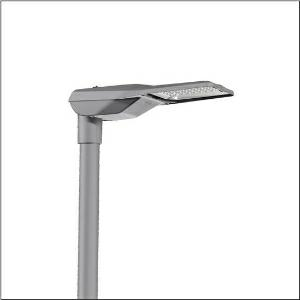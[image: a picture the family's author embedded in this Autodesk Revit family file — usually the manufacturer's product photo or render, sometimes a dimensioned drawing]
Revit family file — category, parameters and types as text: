
# Revit family: streetlight_sl_21_mini___st1_0ab_5xe2m33s08hb_60c9
name_source: partatom
category: Lighting Fixtures
units: mm (PartAtom-declared; Revit-internal decimal feet)

## family parameters
Cut with Voids When Loaded = No
Host = Face
Light Source = No
Part Type = Normal
Room Calculation Point = No
Round Connector Dimension = Use Diameter
Shared = No

## types (1)
- --- (1 x LED, 7960 lm, 66 W, 3000K)
    Apparent Load = 66 VA
    CIE Flux Codes = 38 73 97 100 100
    Color Rendering = 70
    Color Temperature = 3000K
    Default Elevation = 1800 mm
    Description = Streetlight SL 21 mini, mast luminaire, primary light control with lens, of PMMA, primary optical cover: cover, of toughened safety glass, transparent, light distribution: ST1.0aB, light emission: direct distribution, primary light characteristic: asymmetric, installation type: side-entry, post-top, LED, High Power LED, rated luminous flux: 7.960lm, luminous efficacy: 121lm/W, light colour: 730, colour temperature: 3000K, control gear: D4i, control: flexible luminous flux parameterisation, time-dependent luminous flux control, constant luminous flux control, overheat protection, pre-setting: logarithmic dimming characteristic, mains connection: 220..240V, AC, 50/60Hz, start of lifetime: 66W, end of service life: 69W, reduction: 30W, luminaire housing, of diecast aluminium, powder-coated, SITECO metallic grey (DB 702S), corrosivity category C5 high according to DIN EN ISO 12944, please order mast flange separately, inclination adjustable: 0°, 5°, 10°, 15°, sealing non-destructively replaceable, multi-level sealing system, length: 628mm, width: 235mm, height: 110mm, mast flange for spigot size: 42mm (side-entry): 5XC10008XM4, 60/48mm (side-entry/post-top): 5XC10108XM2, 76/60mm (side-entry/post-top): 5XC10108XM1, mounting height: 4..8m, Smart Interface above, protection rating (complete): IP66, insulation class (complete): insulation class II (safety insulation), certification: CE, ENEC, ENEC+, VDE, impact resistance: IK10, permissible operating ambient temperature for outdoor applications: -40..+50°C, standard-compliant lighting for roads and squares, packaging unit: 1 piece

Light Distribution: ST1.0aB
    Height = 110 mm
    Lamp = 1 x LED
    Lamp Light Flux = 7960 lm
    Lamp Power = 66 W
    Lamp count = 1
    Length = 625 mm
    Luminous efficacy = 121 lm/W
    Manufacturer = Siteco
    ModVariant = No
    Model = 5XE2M33S08HB
    Number of Poles = 1
    OnlyDefault = Yes
    Power Factor = 1
    Product Name = Streetlight SL 21 mini | ST1.0aB
    Product group = mast luminaire | pylon top
    ProductGroupID = 6100
    Protection Class = Protection class II
    Protection Degree = IP 66
    RLX_Detail_Level = 1
    RLX_Emergency_Light_Flux = 0 lm
    RLX_Emergency_Type = 0
    RLX_Emergency_Type_DB = No
    RlxData = <blob elided: 26033 chars, md5=1e8d49fc>
    Socket = socket
    Standby Power = 0 W
    System Light Flux = 7960 lm
    System Power = 66 W
    Type Comments = factory setting: luminous flux: 100 % | dim-lin: 254 | 670 mA
    Type Image = l_1003515.jpg
    URL = http://relux.com
    VarID = @adj_180045
    Voltage = 0 V
    Weight = 0.00 kg
    Width = 234 mm

## geometry (parser evidence)
native form markers: Blend x4, Sweep x9
no freeform markers — native parametric forms only
